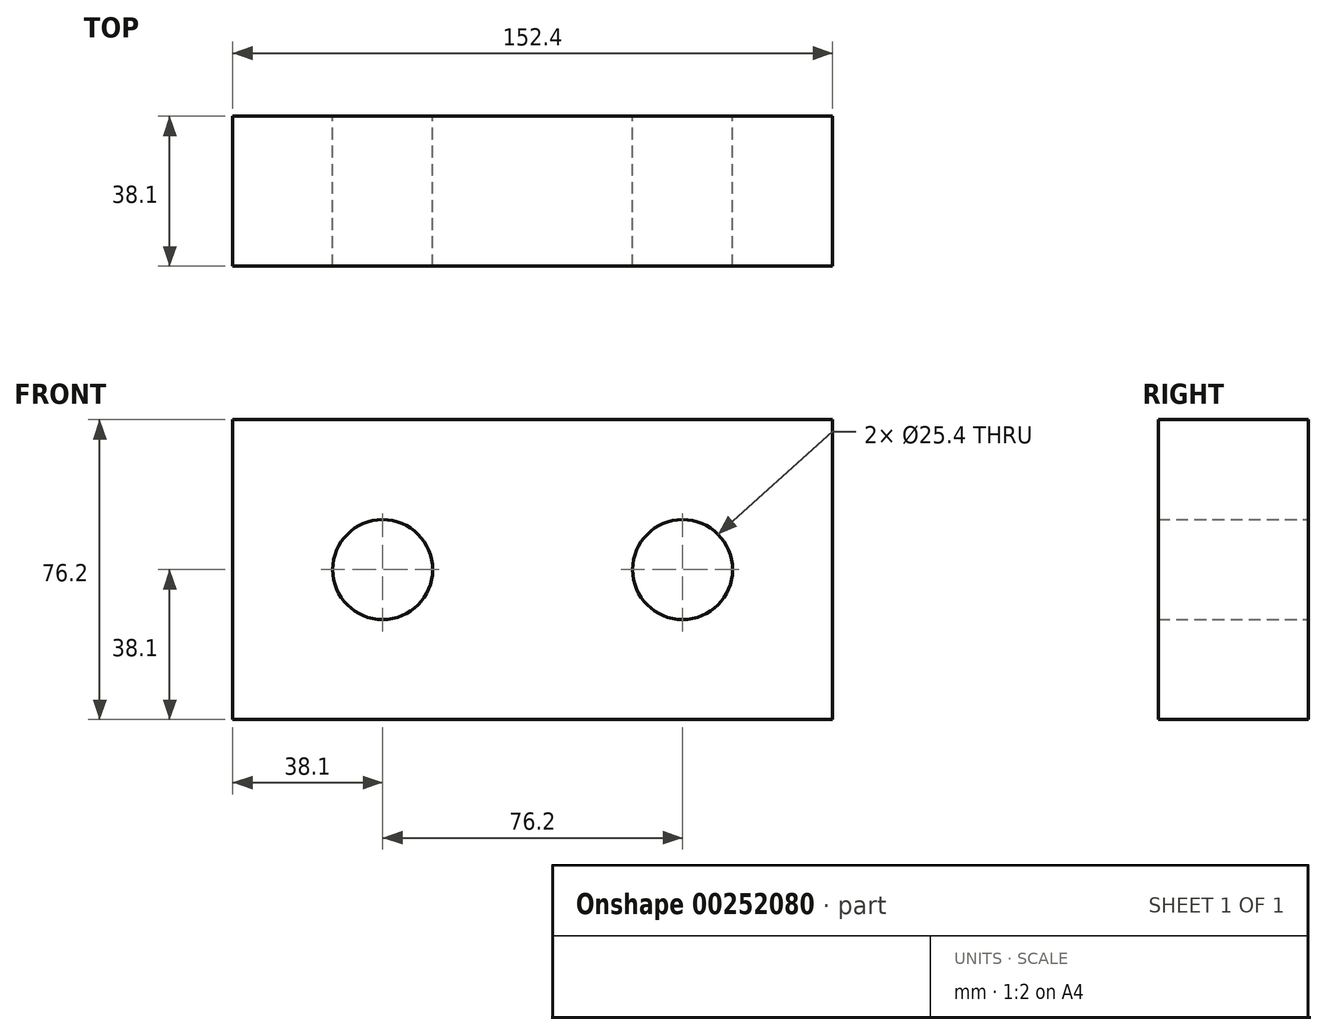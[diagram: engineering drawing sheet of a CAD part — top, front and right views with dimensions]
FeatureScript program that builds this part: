
annotation { "Feature Type Name" : "Feature", "Feature Type Description" : "" }
export const myFeature = defineFeature(function(context is Context, id is Id, definition is map)
    precondition{}
    {
        {
            var Q0;
            Q0=qCreatedBy(makeId("Front.planeOp"),FACE);
            var sketch = newSketch(context, id + "F0", { "sketchPlane" : qUnion([Q0])});
            skLineSegment(sketch, "E0.bottom", {"start": v(76.2, -38.1) * mm, "end": v(-76.2, -38.1) * mm});
            skLineSegment(sketch, "E0.top", {"start": v(76.2, 38.1) * mm, "end": v(-76.2, 38.1) * mm});
            skLineSegment(sketch, "E0.left", {"start": v(76.2, -38.1) * mm, "end": v(76.2, 38.1) * mm});
            skLineSegment(sketch, "E0.right", {"start": v(-76.2, -38.1) * mm, "end": v(-76.2, 38.1) * mm});
            skPoint(sketch, "E0.middle", {"position": v(0, 0) * mm});
            skLineSegment(sketch, "E1", {"start": v(0, 0) * mm, "end": v(38.1, 0) * mm});
            skCircle(sketch, "E2", {"center": v(38.1, 0) * mm, "radius": 12.7 * mm});
            skLineSegment(sketch, "E3", {"start": v(0, 0) * mm, "end": v(-38.1, 0) * mm});
            skCircle(sketch, "E4", {"center": v(-38.1, 0) * mm, "radius": 12.7 * mm});
            skSolve(sketch);
        }
        {
            var Q0;
            Q0 = qSketchRegion(id + "F0", true);
            extrude(context, id + "F1", {"entities" : qUnion([Q0]), "depth" : 38.1 * mm});
        }
    });
